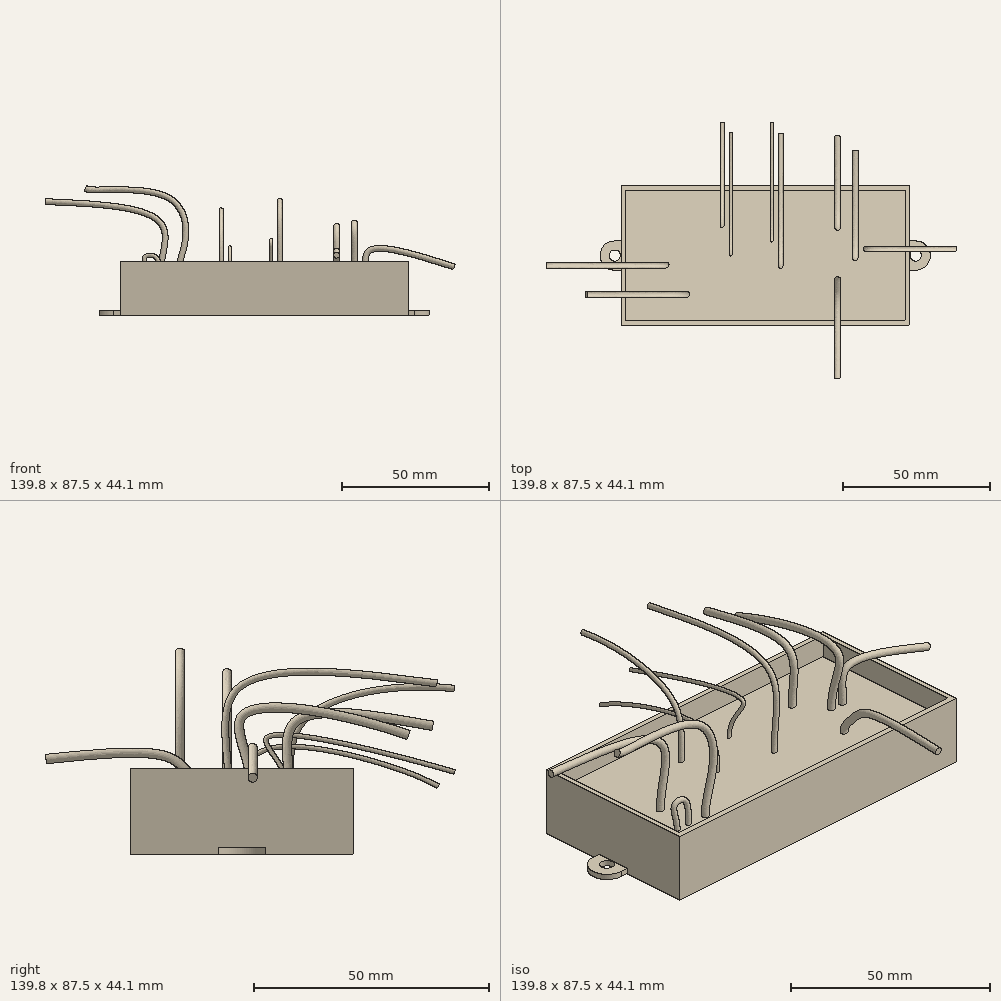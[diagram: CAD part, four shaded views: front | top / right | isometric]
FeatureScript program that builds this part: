
annotation { "Feature Type Name" : "Feature", "Feature Type Description" : "" }
export const myFeature = defineFeature(function(context is Context, id is Id, definition is map)
    precondition{}
    {
        {
            var Q0;
            Q0=qCreatedBy(makeId("Top.planeOp"),FACE);
            var sketch = newSketch(context, id + "F0", { "sketchPlane" : qUnion([Q0])});
            skLineSegment(sketch, "E0.bottom", {"start": v(49.2, -23.75) * mm, "end": v(-49.2, -23.75) * mm});
            skLineSegment(sketch, "E0.top", {"start": v(49.2, 23.75) * mm, "end": v(-49.2, 23.75) * mm});
            skLineSegment(sketch, "E0.left", {"start": v(49.2, -23.75) * mm, "end": v(49.2, 23.75) * mm});
            skLineSegment(sketch, "E0.right", {"start": v(-49.2, -23.75) * mm, "end": v(-49.2, 23.75) * mm});
            skPoint(sketch, "E0.middle", {"position": v(0, 0) * mm});
            skSolve(sketch);
        }
        {
            var Q0;
            Q0 = qSketchRegion(id + "F0", true);
            extrude(context, id + "F1", {"entities" : qUnion([Q0]), "depth" : 18.4 * mm});
        }
        {
            var Q0;
            Q0=makeQuery(id+"F1.opExtrude","CAP_FACE",FACE,{"disambiguationData":[OSD([sQuery(id+"F0.wireOp",EDGE,"E0.bottom"),sQuery(id+"F0.wireOp",EDGE,"E0.top"),sQuery(id+"F0.wireOp",EDGE,"E0.left"),sQuery(id+"F0.wireOp",EDGE,"E0.right")])],"isStart":false});
            shell(context, id + "F2", {"entities" : qUnion([Q0]), "thickness" : 1.5 * mm});
        }
        {
            var Q0;
            Q0=makeQuery(id+"F2.opShell","OFFSET_FACE",FACE,{"disambiguationData":[OSD([sQuery(id+"F0.wireOp",EDGE,"E0.bottom"),sQuery(id+"F0.wireOp",EDGE,"E0.top"),sQuery(id+"F0.wireOp",EDGE,"E0.left"),sQuery(id+"F0.wireOp",EDGE,"E0.right")])]});
            var sketch = newSketch(context, id + "F3", { "sketchPlane" : qUnion([Q0])});
            skLineSegment(sketch, "E1.bottom", {"start": v(47.7, 22.25) * mm, "end": v(-47.7, 22.25) * mm});
            skLineSegment(sketch, "E1.top", {"start": v(47.7, -22.25) * mm, "end": v(-47.7, -22.25) * mm});
            skLineSegment(sketch, "E1.left", {"start": v(47.7, 22.25) * mm, "end": v(47.7, -22.25) * mm});
            skLineSegment(sketch, "E1.right", {"start": v(-47.7, 22.25) * mm, "end": v(-47.7, -22.25) * mm});
            skSolve(sketch);
        }
        {
            var Q0;
            Q0 = qSketchRegion(id + "F3", true);
            extrude(context, id + "F4", {"entities" : qUnion([Q0]), "operationType" : NewBodyOperationType.ADD, "depth" : 10.8 * mm});
        }
        {
            var Q0;
            Q0=qCreatedBy(makeId("Top.planeOp"),FACE);
            var sketch = newSketch(context, id + "F5", { "sketchPlane" : qUnion([Q0])});
            skCircle(sketch, "E2", {"center": v(-51.3, 0) * mm, "radius": 1.9 * mm});
            skCircle(sketch, "E3", {"center": v(51.3, 0) * mm, "radius": 1.9 * mm});
            skArc(sketch, "E4", {"start": v(-51.3, 5) * mm, "mid": v(-56.3, 0) * mm, "end": v(-51.3, -5) * mm});
            skArc(sketch, "E5", {"start": v(51.3, -5) * mm, "mid": v(56.3, 0) * mm, "end": v(51.3, 5) * mm});
            skLineSegment(sketch, "E6", {"start": v(51.3, 5) * mm, "end": v(49.2, 5) * mm});
            skLineSegment(sketch, "E7", {"start": v(49.2, 5) * mm, "end": v(49.2, -5) * mm});
            skLineSegment(sketch, "E8", {"start": v(49.2, -5) * mm, "end": v(51.3, -5) * mm});
            skLineSegment(sketch, "E9", {"start": v(-51.3, 5) * mm, "end": v(-49.2, 5) * mm});
            skLineSegment(sketch, "E10", {"start": v(-49.2, 5) * mm, "end": v(-49.2, -5) * mm});
            skLineSegment(sketch, "E11", {"start": v(-49.2, -5) * mm, "end": v(-51.3, -5) * mm});
            skSolve(sketch);
        }
        {
            var Q0;
            {var subQ2=sQuery(id+"F5.wireOp",EDGE,"E2");Q0=makeQuery(id+"F5.imprint","IMPRINT",FACE,{"disambiguationData":[TD([[makeQuery(id+"F5.imprint","IMPRINT",EDGE,{"derivedFrom":subQ2}),-1.0]])]});}
            extrude(context, id + "F6", {"entities" : qUnion([Q0]), "operationType" : NewBodyOperationType.ADD, "depth" : 1.5 * mm});
        }
        {
            var Q0;
            Q0=makeQuery(id+"F5.imprint","IMPRINT",FACE,{"disambiguationData":[TD([[makeQuery(id+"F5.imprint","IMPRINT",EDGE,{"derivedFrom":sQuery(id+"F5.wireOp",EDGE,"E3")}),-1.0]])]});
            var Q1;
            Q1=sQuery(id+"F5.wireOp",EDGE,"E4");
            var Q2;
            Q2=sQuery(id+"F5.wireOp",EDGE,"E11");
            var Q3;
            Q3=sQuery(id+"F5.wireOp",EDGE,"E10");
            var Q4;
            Q4=sQuery(id+"F5.wireOp",EDGE,"E9");
            var Q5;
            Q5=sQuery(id+"F5.wireOp",EDGE,"E3");
            var Q6;
            Q6=sQuery(id+"F5.wireOp",EDGE,"E6");
            var Q7;
            Q7=sQuery(id+"F5.wireOp",EDGE,"E5");
            var Q8;
            Q8=sQuery(id+"F5.wireOp",EDGE,"E8");
            var Q9;
            Q9=sQuery(id+"F5.wireOp",EDGE,"E7");
            extrude(context, id + "F7", {"entities" : qUnion([Q0]), "operationType" : NewBodyOperationType.ADD, "surfaceEntities" : qUnion([Q1, Q2, Q3, Q4, Q5, Q6, Q7, Q8, Q9]), "depth" : 1.5 * mm});
        }
        {
            var Q0;
            Q0=makeQuery(id+"F4.opExtrude","CAP_FACE",FACE,{"disambiguationData":[OSD([sQuery(id+"F3.wireOp",EDGE,"E1.bottom"),sQuery(id+"F3.wireOp",EDGE,"E1.top"),sQuery(id+"F3.wireOp",EDGE,"E1.left"),sQuery(id+"F3.wireOp",EDGE,"E1.right")])],"isStart":false});
            var sketch = newSketch(context, id + "F8", { "sketchPlane" : qUnion([Q0])});
            skCircle(sketch, "E12", {"center": v(-35.7, -13.25) * mm, "radius": 0.75 * mm});
            skPoint(sketch, "E13", {"position": v(-39.7, -13.25) * mm});
            skSolve(sketch);
        }
        {
            var Q0;
            Q0=qCreatedBy(makeId("Front.planeOp"),FACE);
            var Q1;
            Q1=sQuery(id+"F8.wireOp",VERTEX,"E13");
            cPlane(context, id + "F9", {"entities" : qUnion([Q0, Q1]), "cplaneType" : CPlaneType.PLANE_POINT, "offset" : 25 * mm, "width" : 150 * mm, "height" : 150 * mm});
        }
        {
            var Q0;
            Q0=qCreatedBy(id+"F9.planeOp",FACE);
            var sketch = newSketch(context, id + "F10", { "sketchPlane" : qUnion([Q0])});
            skFitSpline(sketch, "E14", {"points": [v(-39.7, 12.3) * mm, v(-40.63, 19.68) * mm, v(-37.25, 19.92) * mm, v(-35.7, 12.3) * mm], "startDerivative": vector(0, 26.48) * mm, "endDerivative": vector(0, -26.47) * mm});
            skLineSegment(sketch, "E15", {"start": v(-35.7, 12.3) * mm, "end": v(-35.7, 9.38) * mm});
            skLineSegment(sketch, "E16", {"start": v(-39.7, 12.3) * mm, "end": v(-39.7, 8.9) * mm});
            skSolve(sketch);
        }
        {
            var Q0;
            Q0=makeQuery(id+"F8.imprint","IMPRINT",FACE,{"disambiguationData":[TD([[makeQuery(id+"F8.imprint","IMPRINT",EDGE,{"derivedFrom":sQuery(id+"F8.wireOp",EDGE,"E12")}),1.0]])]});
            var Q1;
            Q1=sQuery(id+"F10.wireOp",EDGE,"E14");
            sweep(context, id + "F11", {"profiles" : qUnion([Q0]), "path" : qUnion([Q1])});
        }
        {
            var Q0;
            Q0=makeQuery(id+"F8.imprint","IMPRINT",FACE,{"disambiguationData":[TD([[makeQuery(id+"F8.imprint","IMPRINT",EDGE,{"derivedFrom":sQuery(id+"F8.wireOp",EDGE,"E12")}),-1.0]])]});
            var sketch = newSketch(context, id + "F12", { "sketchPlane" : qUnion([Q0])});
            skCircle(sketch, "E17", {"center": v(-29.7, -13.25) * mm, "radius": 1 * mm});
            skSolve(sketch);
        }
        {
            var Q0;
            Q0=qCreatedBy(id+"F9.planeOp",FACE);
            var sketch = newSketch(context, id + "F13", { "sketchPlane" : qUnion([Q0])});
            skFitSpline(sketch, "E18", {"points": [v(-29.7, 12.3) * mm, v(-26.9, 26.07) * mm, v(-32.95, 40.14) * mm, v(-58.92, 42.7) * mm, v(-61, 43.18) * mm], "startDerivative": vector(0, 50.27) * mm, "endDerivative": vector(-12.03, 5.94) * mm});
            skLineSegment(sketch, "E19", {"start": v(-29.7, 12.3) * mm, "end": v(-29.7, 7.14) * mm});
            skSolve(sketch);
        }
        {
            var Q0;
            Q0=makeQuery(id+"F12.imprint","IMPRINT",FACE,{"disambiguationData":[TD([[makeQuery(id+"F12.imprint","IMPRINT",EDGE,{"derivedFrom":sQuery(id+"F12.wireOp",EDGE,"E17")}),1.0]])]});
            var Q1;
            Q1=sQuery(id+"F13.wireOp",EDGE,"E18");
            sweep(context, id + "F14", {"operationType" : NewBodyOperationType.ADD, "profiles" : qUnion([Q0]), "path" : qUnion([Q1])});
        }
        {
            var Q0;
            Q0=qCreatedBy(id+"F9.planeOp",FACE);
            cPlane(context, id + "F15", {"entities" : qUnion([Q0]), "cplaneType" : CPlaneType.OFFSET, "offset" : 10 * mm, "oppositeDirection" : true, "width" : 150 * mm, "height" : 150 * mm});
        }
        {
            var Q0;
            Q0=makeQuery(id+"F8.imprint","IMPRINT",FACE,{"disambiguationData":[TD([[makeQuery(id+"F8.imprint","IMPRINT",EDGE,{"derivedFrom":sQuery(id+"F8.wireOp",EDGE,"E12")}),-1.0]])]});
            var sketch = newSketch(context, id + "F16", { "sketchPlane" : qUnion([Q0])});
            skCircle(sketch, "E20", {"center": v(-35.7, -3.25) * mm, "radius": 1 * mm});
            skSolve(sketch);
        }
        {
            var Q0;
            Q0=qCreatedBy(id+"F15.planeOp",FACE);
            var sketch = newSketch(context, id + "F17", { "sketchPlane" : qUnion([Q0])});
            skFitSpline(sketch, "E21", {"points": [v(-35.7, 12.3) * mm, v(-34.94, 30.84) * mm, v(-74.59, 38.7) * mm], "startDerivative": vector(0, 50.23) * mm, "endDerivative": vector(-84.23, 3.78) * mm});
            skLineSegment(sketch, "E22", {"start": v(-35.7, 12.3) * mm, "end": v(-35.7, 8.23) * mm, "construction": true});
            skSolve(sketch);
        }
        {
            var Q0;
            Q0 = qSketchRegion(id + "F16", true);
            var Q1;
            Q1 = qConstructionFilter(qBodyType(qCreatedBy(id + "F17" ,EDGE), BodyType.WIRE), ConstructionObject.NO);
            sweep(context, id + "F18", {"profiles" : qUnion([Q0]), "path" : qUnion([Q1])});
        }
        {
            var Q0;
            Q0=makeQuery(id+"F8.imprint","IMPRINT",FACE,{"disambiguationData":[TD([[makeQuery(id+"F8.imprint","IMPRINT",EDGE,{"derivedFrom":sQuery(id+"F8.wireOp",EDGE,"E12")}),-1.0]])]});
            var sketch = newSketch(context, id + "F19", { "sketchPlane" : qUnion([Q0])});
            skCircle(sketch, "E23", {"center": v(-14.7, 10.25) * mm, "radius": 0.7 * mm});
            skCircle(sketch, "E24", {"center": v(2.3, 10.25) * mm, "radius": 0.5 * mm});
            skCircle(sketch, "E25", {"center": v(-11.7, 0.25) * mm, "radius": 0.5 * mm});
            skSolve(sketch);
        }
        {
            var Q0;
            Q0=makeQuery(id+"F1.opExtrude","SWEPT_FACE",FACE,{"disambiguationData":[OSD([sQuery(id+"F0.wireOp",EDGE,"E0.right")])]});
            var Q1;
            Q1=sQuery(id+"F19.wireOp",VERTEX,"E23.center");
            cPlane(context, id + "F20", {"entities" : qUnion([Q0, Q1]), "cplaneType" : CPlaneType.PLANE_POINT, "offset" : 25 * mm, "width" : 150 * mm, "height" : 150 * mm});
        }
        {
            var Q0;
            Q0=makeQuery(id+"F1.opExtrude","SWEPT_FACE",FACE,{"disambiguationData":[OSD([sQuery(id+"F0.wireOp",EDGE,"E0.right")])]});
            var Q1;
            Q1=sQuery(id+"F19.wireOp",VERTEX,"E25.center");
            cPlane(context, id + "F21", {"entities" : qUnion([Q0, Q1]), "cplaneType" : CPlaneType.PLANE_POINT, "offset" : 25 * mm, "width" : 150 * mm, "height" : 150 * mm});
        }
        {
            var Q0;
            Q0=qCreatedBy(id+"F21.planeOp",FACE);
            var Q1;
            Q1=sQuery(id+"F19.wireOp",VERTEX,"E24.center");
            cPlane(context, id + "F22", {"entities" : qUnion([Q0, Q1]), "cplaneType" : CPlaneType.PLANE_POINT, "offset" : 25 * mm, "width" : 150 * mm, "height" : 150 * mm});
        }
        {
            var Q0;
            Q0=qCreatedBy(id+"F20.planeOp",FACE);
            var sketch = newSketch(context, id + "F23", { "sketchPlane" : qUnion([Q0])});
            skFitSpline(sketch, "E26", {"points": [v(-10.25, 12.3) * mm, v(-13.23, 28.6) * mm, v(-45.3, 35.46) * mm], "startDerivative": vector(0, 51.42) * mm, "endDerivative": vector(-68.01, -7.59) * mm});
            skLineSegment(sketch, "E27", {"start": v(-10.25, 12.3) * mm, "end": v(-10.25, 9.59) * mm, "construction": true});
            skSolve(sketch);
        }
        {
            var Q0;
            Q0=makeQuery(id+"F19.imprint","IMPRINT",FACE,{"disambiguationData":[TD([[makeQuery(id+"F19.imprint","IMPRINT",EDGE,{"derivedFrom":sQuery(id+"F19.wireOp",EDGE,"E23")}),1.0]])]});
            var Q1;
            Q1=sQuery(id+"F23.wireOp",EDGE,"E26");
            sweep(context, id + "F24", {"profiles" : qUnion([Q0]), "path" : qUnion([Q1])});
        }
        {
            var Q0;
            Q0=qCreatedBy(id+"F21.planeOp",FACE);
            var sketch = newSketch(context, id + "F25", { "sketchPlane" : qUnion([Q0])});
            skFitSpline(sketch, "E28", {"points": [v(-0.25, 12.3) * mm, v(-4.72, 22.28) * mm, v(-34.23, 17.96) * mm, v(-41.85, 14.61) * mm], "startDerivative": vector(0, 46.45) * mm, "endDerivative": vector(-19.64, -9.82) * mm});
            skLineSegment(sketch, "E29", {"start": v(-0.25, 12.3) * mm, "end": v(-0.25, 8.92) * mm, "construction": true});
            skSolve(sketch);
        }
        {
            var Q0;
            Q0=makeQuery(id+"F19.imprint","IMPRINT",FACE,{"disambiguationData":[TD([[makeQuery(id+"F19.imprint","IMPRINT",EDGE,{"derivedFrom":sQuery(id+"F19.wireOp",EDGE,"E25")}),1.0]])]});
            var Q1;
            Q1=sQuery(id+"F25.wireOp",EDGE,"E28");
            sweep(context, id + "F26", {"profiles" : qUnion([Q0]), "path" : qUnion([Q1])});
        }
        {
            var Q0;
            Q0=qCreatedBy(id+"F22.planeOp",FACE);
            var sketch = newSketch(context, id + "F27", { "sketchPlane" : qUnion([Q0])});
            skFitSpline(sketch, "E30", {"points": [v(-10.23, 12.31) * mm, v(-5.1, 24.62) * mm, v(-45.36, 17.68) * mm], "startDerivative": vector(0, 50.58) * mm, "endDerivative": vector(-87.9, -25.14) * mm});
            skLineSegment(sketch, "E31", {"start": v(-10.23, 12.31) * mm, "end": v(-10.23, 8.6) * mm, "construction": true});
            skSolve(sketch);
        }
        {
            var Q0;
            Q0=makeQuery(id+"F19.imprint","IMPRINT",FACE,{"disambiguationData":[TD([[makeQuery(id+"F19.imprint","IMPRINT",EDGE,{"derivedFrom":sQuery(id+"F19.wireOp",EDGE,"E24")}),1.0]])]});
            var Q1;
            Q1=sQuery(id+"F27.wireOp",EDGE,"E30");
            sweep(context, id + "F28", {"profiles" : qUnion([Q0]), "path" : qUnion([Q1])});
        }
        {
            var Q0;
            Q0=qCreatedBy(id+"F22.planeOp",FACE);
            cPlane(context, id + "F29", {"entities" : qUnion([Q0]), "cplaneType" : CPlaneType.OFFSET, "offset" : 3 * mm, "oppositeDirection" : true, "width" : 150 * mm, "height" : 150 * mm});
        }
        {
            var Q0;
            Q0=makeQuery(id+"F19.imprint","IMPRINT",FACE,{"disambiguationData":[TD([[makeQuery(id+"F19.imprint","IMPRINT",EDGE,{"derivedFrom":sQuery(id+"F19.wireOp",EDGE,"E23")}),-1.0]])]});
            var sketch = newSketch(context, id + "F30", { "sketchPlane" : qUnion([Q0])});
            skCircle(sketch, "E32", {"center": v(5.3, -2.75) * mm, "radius": 0.75 * mm});
            skSolve(sketch);
        }
        {
            var Q0;
            Q0=qCreatedBy(id+"F29.planeOp",FACE);
            var sketch = newSketch(context, id + "F31", { "sketchPlane" : qUnion([Q0])});
            skFitSpline(sketch, "E33", {"points": [v(2.75, 12.3) * mm, v(1.24, 35.1) * mm, v(-41.54, 36.58) * mm], "startDerivative": vector(0, 63.72) * mm, "endDerivative": vector(-92.47, -12.02) * mm});
            skLineSegment(sketch, "E34", {"start": v(2.75, 12.3) * mm, "end": v(2.75, 6.45) * mm, "construction": true});
            skSolve(sketch);
        }
        {
            var Q0;
            Q0=makeQuery(id+"F30.imprint","IMPRINT",FACE,{"disambiguationData":[TD([[makeQuery(id+"F30.imprint","IMPRINT",EDGE,{"derivedFrom":sQuery(id+"F30.wireOp",EDGE,"E32")}),1.0]])]});
            var Q1;
            Q1=sQuery(id+"F31.wireOp",EDGE,"E33");
            sweep(context, id + "F32", {"profiles" : qUnion([Q0]), "path" : qUnion([Q1])});
        }
        {
            var Q0;
            Q0=makeQuery(id+"F2.opShell","OFFSET_FACE",FACE,{"disambiguationData":[OSD([sQuery(id+"F0.wireOp",EDGE,"E0.left")])]});
            cPlane(context, id + "F33", {"entities" : qUnion([Q0]), "cplaneType" : CPlaneType.OFFSET, "offset" : 23 * mm, "width" : 150 * mm, "height" : 150 * mm});
        }
        {
            var Q0;
            Q0=makeQuery(id+"F19.imprint","IMPRINT",FACE,{"disambiguationData":[TD([[makeQuery(id+"F19.imprint","IMPRINT",EDGE,{"derivedFrom":sQuery(id+"F19.wireOp",EDGE,"E23")}),-1.0]])]});
            var sketch = newSketch(context, id + "F34", { "sketchPlane" : qUnion([Q0])});
            skCircle(sketch, "E35", {"center": v(24.7, -8.25) * mm, "radius": 1 * mm});
            skSolve(sketch);
        }
        {
            var Q0;
            Q0=qCreatedBy(id+"F33.planeOp",FACE);
            var sketch = newSketch(context, id + "F35", { "sketchPlane" : qUnion([Q0])});
            skFitSpline(sketch, "E36", {"points": [v(8.25, 12.3) * mm, v(11.33, 17.32) * mm, v(16.31, 21.01) * mm, v(41.89, 20.41) * mm], "startDerivative": vector(0, 23.21) * mm, "endDerivative": vector(59.06, -6.04) * mm});
            skLineSegment(sketch, "E37", {"start": v(8.25, 12.3) * mm, "end": v(8.25, 6.96) * mm, "construction": true});
            skSolve(sketch);
        }
        {
            var Q0;
            Q0 = qSketchRegion(id + "F34", true);
            var Q1;
            Q1 = qSketchRegion(id + "F34", true);
            var Q2;
            Q2 = qConstructionFilter(qBodyType(qCreatedBy(id + "F35" ,EDGE), BodyType.WIRE), ConstructionObject.NO);
            var Q3;
            Q3 = qConstructionFilter(qBodyType(qCreatedBy(id + "F35" ,EDGE), BodyType.WIRE), ConstructionObject.NO);
            sweep(context, id + "F36", {"profiles" : qUnion([Q0, Q1]), "path" : qUnion([Q2, Q3])});
        }
        {
            var Q0;
            Q0=makeQuery(id+"F19.imprint","IMPRINT",FACE,{"disambiguationData":[TD([[makeQuery(id+"F19.imprint","IMPRINT",EDGE,{"derivedFrom":sQuery(id+"F19.wireOp",EDGE,"E23")}),-1.0]])]});
            cPlane(context, id + "F37", {"entities" : qUnion([Q0]), "cplaneType" : CPlaneType.OFFSET, "offset" : 0 * mm, "width" : 150 * mm, "height" : 150 * mm});
        }
        {
            var Q0;
            Q0=qCreatedBy(id+"F37.planeOp",FACE);
            var sketch = newSketch(context, id + "F38", { "sketchPlane" : qUnion([Q0])});
            skCircle(sketch, "E38", {"center": v(24.7, 10.25) * mm, "radius": 1 * mm});
            skSolve(sketch);
        }
        {
            var Q0;
            Q0=qCreatedBy(id+"F33.planeOp",FACE);
            var sketch = newSketch(context, id + "F39", { "sketchPlane" : qUnion([Q0])});
            skFitSpline(sketch, "E39", {"points": [v(-10.25, 12.3) * mm, v(-11.06, 28.04) * mm, v(-40.66, 27.51) * mm], "startDerivative": vector(0, 43.87) * mm, "endDerivative": vector(-65.45, -11.42) * mm});
            skLineSegment(sketch, "E40", {"start": v(-10.25, 12.3) * mm, "end": v(-10.25, 7.92) * mm, "construction": true});
            skSolve(sketch);
        }
        {
            var Q0;
            Q0 = qSketchRegion(id + "F38", true);
            var Q1;
            Q1 = qConstructionFilter(qBodyType(qCreatedBy(id + "F39" ,EDGE), BodyType.WIRE), ConstructionObject.NO);
            sweep(context, id + "F40", {"profiles" : qUnion([Q0]), "path" : qUnion([Q1])});
        }
        {
            var Q0;
            Q0=makeQuery(id+"F2.opShell","OFFSET_FACE",FACE,{"disambiguationData":[OSD([sQuery(id+"F0.wireOp",EDGE,"E0.top")])]});
            cPlane(context, id + "F41", {"entities" : qUnion([Q0]), "cplaneType" : CPlaneType.OFFSET, "offset" : 20 * mm, "width" : 150 * mm, "height" : 150 * mm});
        }
        {
            var Q0;
            Q0=makeQuery(id+"F19.imprint","IMPRINT",FACE,{"disambiguationData":[TD([[makeQuery(id+"F19.imprint","IMPRINT",EDGE,{"derivedFrom":sQuery(id+"F19.wireOp",EDGE,"E23")}),-1.0]])]});
            var sketch = newSketch(context, id + "F42", { "sketchPlane" : qUnion([Q0])});
            skCircle(sketch, "E41", {"center": v(30.7, 2.25) * mm, "radius": 1 * mm});
            skSolve(sketch);
        }
        {
            var Q0;
            Q0=makeQuery(id+"F19.imprint","IMPRINT",FACE,{"disambiguationData":[TD([[makeQuery(id+"F19.imprint","IMPRINT",EDGE,{"derivedFrom":sQuery(id+"F19.wireOp",EDGE,"E23")}),-1.0]])]});
            var sketch = newSketch(context, id + "F43", { "sketchPlane" : qUnion([Q0])});
            skCircle(sketch, "E42", {"center": v(34.7, 2.25) * mm, "radius": 1 * mm});
            skSolve(sketch);
        }
        {
            var Q0;
            Q0=qCreatedBy(id+"F41.planeOp",FACE);
            var sketch = newSketch(context, id + "F44", { "sketchPlane" : qUnion([Q0])});
            skFitSpline(sketch, "E43", {"points": [v(34.7, 12.3) * mm, v(35.67, 21.8) * mm, v(64.88, 16.42) * mm], "startDerivative": vector(0, 33.49) * mm, "endDerivative": vector(60.71, -19.32) * mm});
            skLineSegment(sketch, "E44", {"start": v(34.7, 12.3) * mm, "end": v(34.7, 5.18) * mm, "construction": true});
            skSolve(sketch);
        }
        {
            var Q0;
            Q0 = qSketchRegion(id + "F43", true);
            var Q1;
            Q1 = qConstructionFilter(qBodyType(qCreatedBy(id + "F44" ,EDGE), BodyType.WIRE), ConstructionObject.NO);
            sweep(context, id + "F45", {"profiles" : qUnion([Q0]), "path" : qUnion([Q1])});
        }
        {
            var Q0;
            Q0=makeQuery(id+"F2.opShell","OFFSET_FACE",FACE,{"disambiguationData":[OSD([sQuery(id+"F0.wireOp",EDGE,"E0.left")])]});
            var Q1;
            Q1=sQuery(id+"F42.wireOp",VERTEX,"E41.center");
            cPlane(context, id + "F46", {"entities" : qUnion([Q0, Q1]), "cplaneType" : CPlaneType.PLANE_POINT, "offset" : 25 * mm, "width" : 150 * mm, "height" : 150 * mm});
        }
        {
            var Q0;
            Q0=qCreatedBy(id+"F46.planeOp",FACE);
            var sketch = newSketch(context, id + "F47", { "sketchPlane" : qUnion([Q0])});
            skFitSpline(sketch, "E45", {"points": [v(-2.25, 12.3) * mm, v(0, 29.52) * mm, v(-35.54, 25.53) * mm], "startDerivative": vector(0, 57.76) * mm, "endDerivative": vector(-72.53, -25.05) * mm});
            skLineSegment(sketch, "E46", {"start": v(-2.25, 12.3) * mm, "end": v(-2.25, 8) * mm, "construction": true});
            skSolve(sketch);
        }
        {
            var Q0;
            Q0 = qSketchRegion(id + "F42", true);
            var Q1;
            Q1 = qConstructionFilter(qBodyType(qCreatedBy(id + "F47" ,EDGE), BodyType.WIRE), ConstructionObject.NO);
            sweep(context, id + "F48", {"profiles" : qUnion([Q0]), "path" : qUnion([Q1])});
        }
    });
